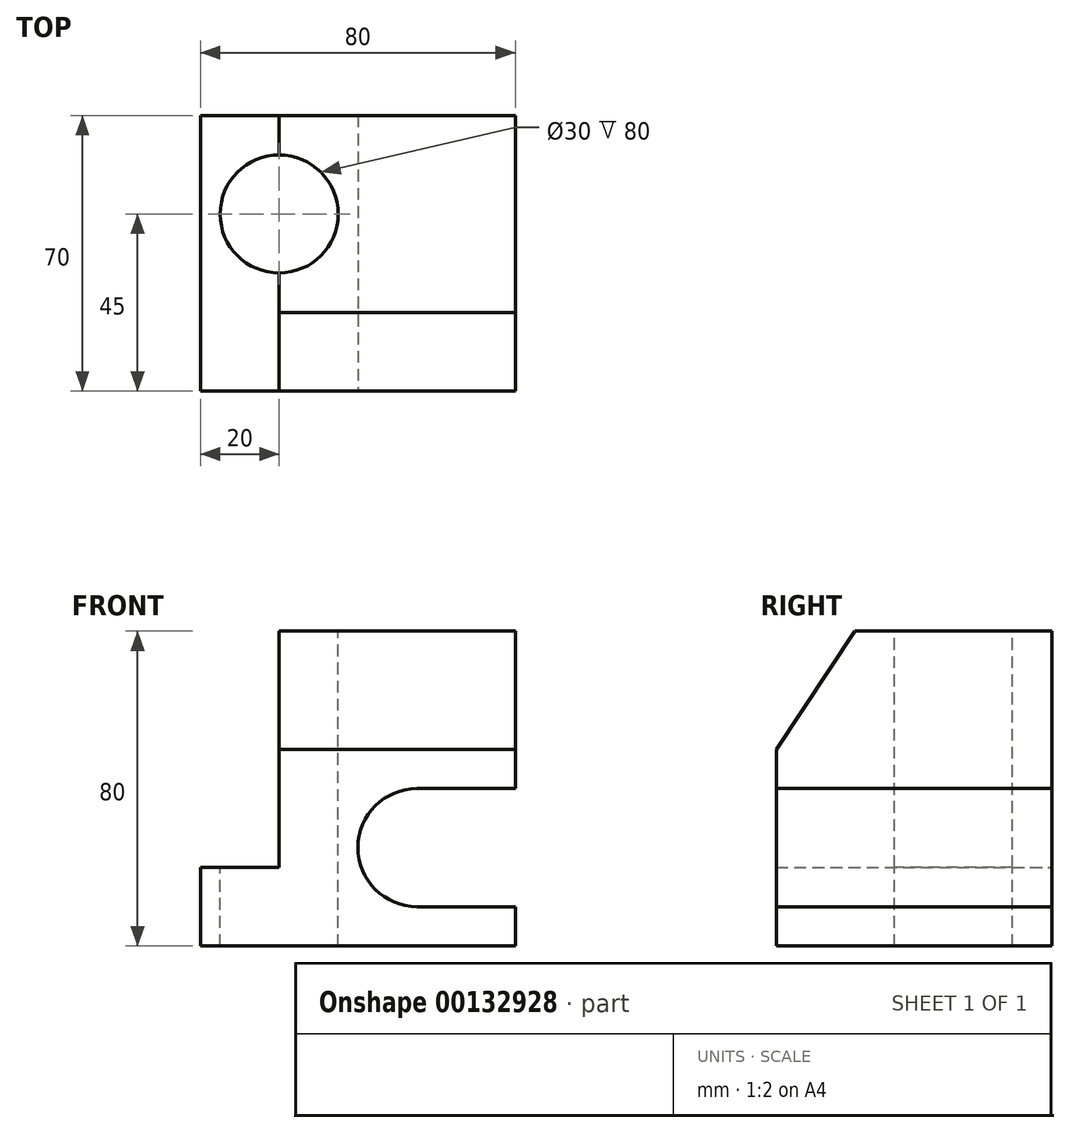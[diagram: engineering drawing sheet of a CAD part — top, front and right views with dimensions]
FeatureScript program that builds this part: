
annotation { "Feature Type Name" : "Feature", "Feature Type Description" : "" }
export const myFeature = defineFeature(function(context is Context, id is Id, definition is map)
    precondition{}
    {
        {
            var Q0;
            Q0=qCreatedBy(makeId("Front.planeOp"),FACE);
            var sketch = newSketch(context, id + "F0", { "sketchPlane" : qUnion([Q0])});
            skLineSegment(sketch, "E0", {"start": v(0, 0) * mm, "end": v(0, 20) * mm});
            skLineSegment(sketch, "E1", {"start": v(0, 20) * mm, "end": v(20, 20) * mm});
            skLineSegment(sketch, "E2", {"start": v(20, 20) * mm, "end": v(20, 80) * mm});
            skLineSegment(sketch, "E3", {"start": v(20, 80) * mm, "end": v(80, 80) * mm});
            skLineSegment(sketch, "E4", {"start": v(80, 80) * mm, "end": v(80, 0) * mm});
            skLineSegment(sketch, "E5", {"start": v(80, 0) * mm, "end": v(0, 0) * mm});
            skSolve(sketch);
        }
        {
            var Q0;
            Q0 = qSketchRegion(id + "F0", true);
            extrude(context, id + "F1", {"entities" : qUnion([Q0]), "endBound" : BoundingType.SYMMETRIC, "depth" : 70 * mm});
        }
        {
            var Q0;
            Q0=makeQuery(id+"F1.opExtrude","CAP_FACE",FACE,{"disambiguationData":[OSD([sQuery(id+"F0.wireOp",EDGE,"E0"),sQuery(id+"F0.wireOp",EDGE,"E1"),sQuery(id+"F0.wireOp",EDGE,"E2"),sQuery(id+"F0.wireOp",EDGE,"E3"),sQuery(id+"F0.wireOp",EDGE,"E4"),sQuery(id+"F0.wireOp",EDGE,"E5")])],"isStart":false});
            var sketch = newSketch(context, id + "F2", { "sketchPlane" : qUnion([Q0])});
            skArc(sketch, "E6", {"start": v(55, 40) * mm, "mid": v(40, 25) * mm, "end": v(55, 10) * mm});
            skLineSegment(sketch, "E7.bottom", {"start": v(80, 40) * mm, "end": v(55, 40) * mm});
            skLineSegment(sketch, "E7.top", {"start": v(80, 10) * mm, "end": v(55, 10) * mm});
            skLineSegment(sketch, "E7.left", {"start": v(80, 40) * mm, "end": v(80, 10) * mm});
            skSolve(sketch);
        }
        {
            var Q0;
            Q0=makeQuery(id+"F2.imprint","IMPRINT",FACE,{"disambiguationData":[TD([[makeQuery(id+"F2.imprint","IMPRINT",EDGE,{"derivedFrom":sQuery(id+"F2.wireOp",EDGE,"E6")}),1.0]])]});
            extrude(context, id + "F3", {"entities" : qUnion([Q0]), "operationType" : NewBodyOperationType.REMOVE, "endBound" : BoundingType.UP_TO_NEXT, "oppositeDirection" : true, "depth" : 25 * mm});
        }
        {
            var Q0;
            Q0=makeQuery(id+"F1.opExtrude","SWEPT_FACE",FACE,{"disambiguationData":[OSD([sQuery(id+"F0.wireOp",EDGE,"E3")])]});
            var sketch = newSketch(context, id + "F4", { "sketchPlane" : qUnion([Q0])});
            skCircle(sketch, "E8", {"center": v(20, 10) * mm, "radius": 15 * mm});
            skSolve(sketch);
        }
        {
            var Q0;
            Q0 = qSketchRegion(id + "F4", true);
            extrude(context, id + "F5", {"entities" : qUnion([Q0]), "operationType" : NewBodyOperationType.REMOVE, "endBound" : BoundingType.THROUGH_ALL, "oppositeDirection" : true, "depth" : 25 * mm});
        }
        {
            var Q0;
            {var subQ0=sQuery(id+"F0.wireOp",EDGE,"E3");var subQ1=sQuery(id+"F0.wireOp",EDGE,"E2");var subQ2=sQuery(id+"F0.wireOp",EDGE,"E1");Q0=makeQuery(id+"F5.boolean.opBoolean","SPLIT",FACE,{"disambiguationData":[TD([makeQuery(id+"F1.opExtrude","CAP_FACE",FACE,{"disambiguationData":[OSD([sQuery(id+"F0.wireOp",EDGE,"E0"),subQ2,subQ1,subQ0,sQuery(id+"F0.wireOp",EDGE,"E4"),sQuery(id+"F0.wireOp",EDGE,"E5")])],"isStart":false})])],"derivedFrom":makeQuery(id+"F1.opExtrude","SWEPT_FACE",FACE,{"disambiguationData":[OSD([subQ1])]})});}
            var sketch = newSketch(context, id + "F6", { "sketchPlane" : qUnion([Q0])});
            skLineSegment(sketch, "E9", {"start": v(15, 80) * mm, "end": v(35, 50) * mm});
            skLineSegment(sketch, "E10", {"start": v(35, 50) * mm, "end": v(35, 80) * mm});
            skLineSegment(sketch, "E11", {"start": v(35, 80) * mm, "end": v(15, 80) * mm});
            skSolve(sketch);
        }
        {
            var Q0;
            Q0=makeQuery(id+"F6.imprint","IMPRINT",FACE,{"disambiguationData":[TD([[makeQuery(id+"F6.imprint","IMPRINT",EDGE,{"derivedFrom":sQuery(id+"F6.wireOp",EDGE,"E9")}),1.0]])]});
            extrude(context, id + "F7", {"entities" : qUnion([Q0]), "operationType" : NewBodyOperationType.REMOVE, "endBound" : BoundingType.THROUGH_ALL, "oppositeDirection" : true, "depth" : 25 * mm});
        }
    });
